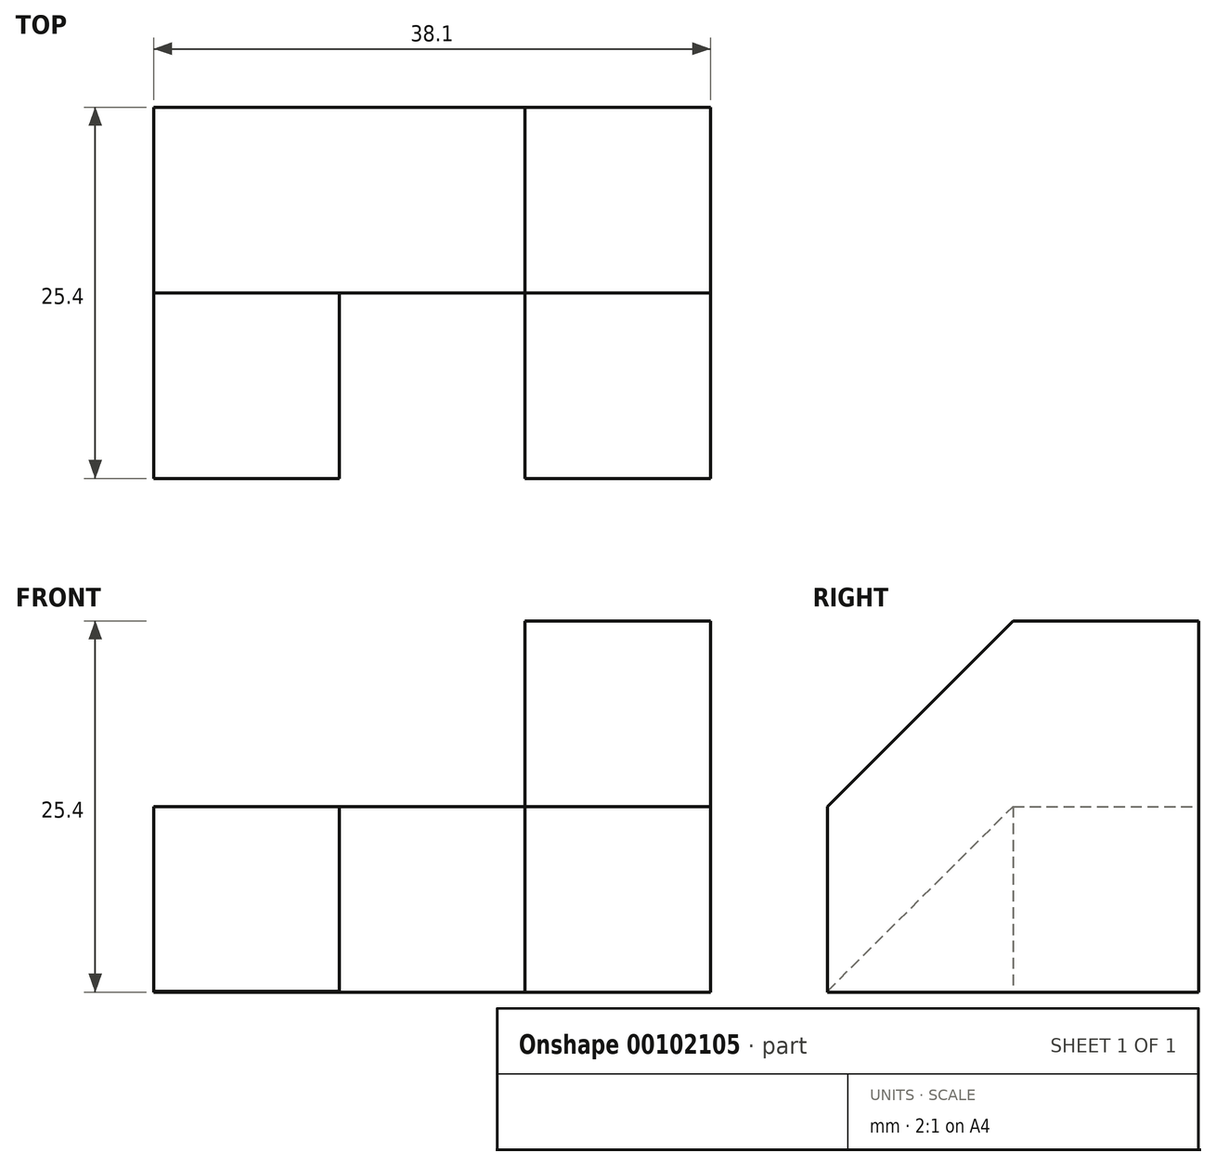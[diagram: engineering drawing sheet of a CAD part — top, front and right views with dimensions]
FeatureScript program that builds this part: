
annotation { "Feature Type Name" : "Feature", "Feature Type Description" : "" }
export const myFeature = defineFeature(function(context is Context, id is Id, definition is map)
    precondition{}
    {
        {
            var Q0;
            Q0=qCreatedBy(makeId("Front.planeOp"),FACE);
            var sketch = newSketch(context, id + "F0", { "sketchPlane" : qUnion([Q0])});
            skLineSegment(sketch, "E0.bottom", {"start": v(0, 0) * mm, "end": v(38.1, 0) * mm});
            skLineSegment(sketch, "E0.top", {"start": v(0, 12.7) * mm, "end": v(38.1, 12.7) * mm});
            skLineSegment(sketch, "E0.left", {"start": v(0, 0) * mm, "end": v(0, 12.7) * mm});
            skLineSegment(sketch, "E0.right", {"start": v(38.1, 0) * mm, "end": v(38.1, 12.7) * mm});
            skLineSegment(sketch, "E1.bottom", {"start": v(38.1, 12.7) * mm, "end": v(25.4, 12.7) * mm});
            skLineSegment(sketch, "E1.top", {"start": v(38.1, 25.4) * mm, "end": v(25.4, 25.4) * mm});
            skLineSegment(sketch, "E1.left", {"start": v(38.1, 12.7) * mm, "end": v(38.1, 25.4) * mm});
            skLineSegment(sketch, "E1.right", {"start": v(25.4, 12.7) * mm, "end": v(25.4, 25.4) * mm});
            skSolve(sketch);
        }
        {
            var Q0;
            Q0 = qSketchRegion(id + "F0", true);
            extrude(context, id + "F1", {"entities" : qUnion([Q0]), "endBound" : BoundingType.SYMMETRIC, "depth" : 25.4 * mm});
        }
        {
            var Q0;
            Q0=qCreatedBy(makeId("Right.planeOp"),FACE);
            var sketch = newSketch(context, id + "F2", { "sketchPlane" : qUnion([Q0])});
            skLineSegment(sketch, "E2", {"start": v(-12.7, 12.7) * mm, "end": v(0, 25.4) * mm});
            skLineSegment(sketch, "E3", {"start": v(0, 25.4) * mm, "end": v(-12.7, 25.4) * mm});
            skLineSegment(sketch, "E4", {"start": v(-12.7, 25.4) * mm, "end": v(-12.7, 12.7) * mm});
            skSolve(sketch);
        }
        {
            var Q0;
            Q0=makeQuery(id+"F2.imprint","IMPRINT",FACE,{"disambiguationData":[TD([[makeQuery(id+"F2.imprint","IMPRINT",EDGE,{"derivedFrom":sQuery(id+"F2.wireOp",EDGE,"E2")}),1.0]])]});
            extrude(context, id + "F3", {"entities" : qUnion([Q0]), "operationType" : NewBodyOperationType.REMOVE, "endBound" : BoundingType.THROUGH_ALL, "depth" : 25.4 * mm});
        }
        {
            var Q0;
            Q0=qCreatedBy(makeId("Top.planeOp"),FACE);
            var sketch = newSketch(context, id + "F4", { "sketchPlane" : qUnion([Q0])});
            skLineSegment(sketch, "E5.bottom", {"start": v(25.4, 0) * mm, "end": v(12.7, 0) * mm});
            skLineSegment(sketch, "E5.top", {"start": v(25.4, -12.7) * mm, "end": v(12.7, -12.7) * mm});
            skLineSegment(sketch, "E5.left", {"start": v(25.4, 0) * mm, "end": v(25.4, -12.7) * mm});
            skLineSegment(sketch, "E5.right", {"start": v(12.7, 0) * mm, "end": v(12.7, -12.7) * mm});
            skLineSegment(sketch, "E6", {"start": v(12.7, -12.7) * mm, "end": v(0, -12.7) * mm});
            skSolve(sketch);
        }
        {
            var Q0;
            Q0=makeQuery(id+"F4.imprint","IMPRINT",FACE,{"disambiguationData":[TD([[makeQuery(id+"F4.imprint","IMPRINT",EDGE,{"derivedFrom":sQuery(id+"F4.wireOp",EDGE,"E5.bottom")}),1.0]])]});
            extrude(context, id + "F5", {"entities" : qUnion([Q0]), "operationType" : NewBodyOperationType.REMOVE, "depth" : 25.4 * mm});
        }
        {
            var Q0;
            Q0=qCreatedBy(makeId("Right.planeOp"),FACE);
            var sketch = newSketch(context, id + "F6", { "sketchPlane" : qUnion([Q0])});
            skLineSegment(sketch, "E7", {"start": v(-12.76, 0) * mm, "end": v(0, 12.7) * mm});
            skLineSegment(sketch, "E8", {"start": v(0, 12.7) * mm, "end": v(-12.7, 12.7) * mm});
            skLineSegment(sketch, "E9", {"start": v(-12.7, 12.7) * mm, "end": v(-12.76, 0) * mm});
            skSolve(sketch);
        }
        {
            var Q0;
            Q0=makeQuery(id+"F6.imprint","IMPRINT",FACE,{"disambiguationData":[TD([[makeQuery(id+"F6.imprint","IMPRINT",EDGE,{"derivedFrom":sQuery(id+"F6.wireOp",EDGE,"E7")}),1.0]])]});
            extrude(context, id + "F7", {"entities" : qUnion([Q0]), "operationType" : NewBodyOperationType.REMOVE, "depth" : 12.7 * mm});
        }
    });
